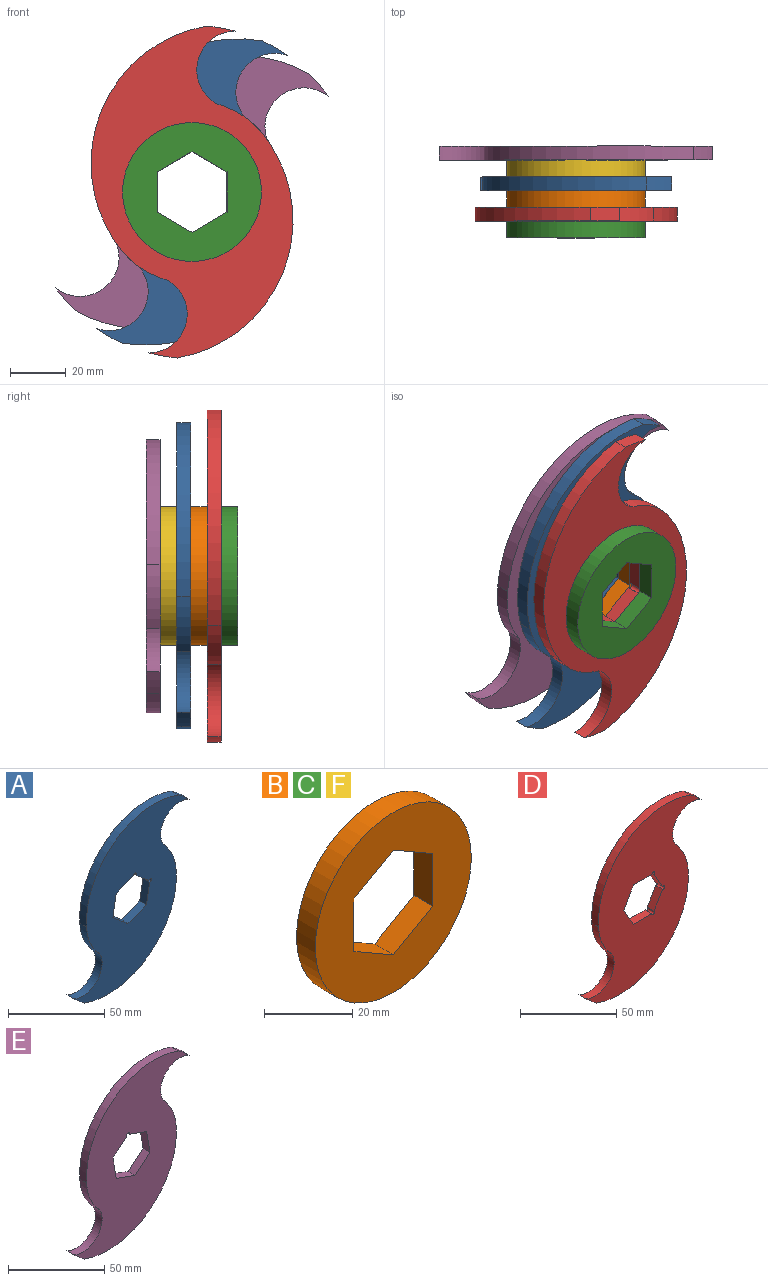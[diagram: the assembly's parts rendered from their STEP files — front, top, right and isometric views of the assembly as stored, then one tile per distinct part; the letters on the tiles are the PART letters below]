
ASSEMBLY  parts=6 mates=4
PART A: 18 faces, bbox 84.9x5x104.4 mm
  f0: plane 9.61x8.07mm, normal (-0.64,0,-0.77), area 62.7mm2, adj f1,f15,f16,f17
  f1: cylinder r=1mm len=5mm, axis (0,1,0), area 20.9mm2, adj f0,f2,f16,f17
  f2: plane 13.34x5mm, normal (-0.98,0,0.17), area 67.7mm2, adj f1,f3,f16,f17
  f3: plane 13.67x5mm, normal (-0.34,0,0.94), area 72.7mm2, adj f2,f4,f16,f17
  f4: plane 11.15x9.35mm, normal (0.64,0,0.77), area 72.7mm2, adj f3,f5,f16,f17
  f5: plane 14.33x5mm, normal (0.98,0,-0.17), area 72.7mm2, adj f4,f6,f16,f17
  f6: plane 12.73x5mm, normal (0.34,0,-0.94), area 67.7mm2, adj f5,f15,f16,f17
  f7: cylinder r=50.21mm len=67.52mm, axis (0,1,0), area 500.3mm2, adj f8,f14,f16,f17
  f8: cylinder r=33mm len=21.82mm, axis (0,1,0), area 122mm2, adj f7,f9,f16,f17
  f9: cylinder r=14.04mm len=20.86mm, axis (0,1,0), area 181.5mm2, adj f8,f10,f16,f17
  f10: cylinder r=60mm len=8mm, axis (0,1,0), area 52.3mm2, adj f9,f11,f16,f17
  f11: cylinder r=50.21mm len=67.52mm, axis (0,1,0), area 500.3mm2, adj f10,f12,f16,f17
  f12: cylinder r=33mm len=21.82mm, axis (0,1,0), area 122mm2, adj f11,f13,f16,f17
  f13: cylinder r=14.04mm len=20.86mm, axis (0,1,0), area 181.5mm2, adj f12,f14,f16,f17
  f14: cylinder r=60mm len=8mm, axis (0,1,0), area 52.3mm2, adj f7,f13,f16,f17
  f15: cylinder r=1mm len=5mm, axis (0,1,0), area 20.9mm2, adj f0,f6,f16,f17
  f16: plane 104.43x84.85mm, normal (0,-1,0), area 4764.9mm2, adj f0,f1,f2,f3,f4,f5,f6,f7
  f17: plane 104.43x84.85mm, normal (0,1,0), area 4764.9mm2, adj f0,f1,f2,f3,f4,f5,f6,f7
PART B: 9 faces, bbox 50x6x50 mm
  f0: plane 12.6x7.27mm, normal (0.5,0,-0.87), area 87.3mm2, adj f1,f6,f7,f8
  f1: plane 12.6x7.27mm, normal (-0.5,0,-0.87), area 87.3mm2, adj f0,f2,f7,f8
  f2: plane 14.55x6mm, normal (-1,0,0), area 87.3mm2, adj f1,f3,f7,f8
  f3: plane 12.6x7.27mm, normal (-0.5,0,0.87), area 87.3mm2, adj f2,f4,f7,f8
  f4: plane 12.6x7.27mm, normal (0.5,0,0.87), area 87.3mm2, adj f3,f6,f7,f8
  f5: cylinder r=25mm len=50mm, axis (0,1,0), area 942.5mm2, adj f7,f8
  f6: plane 14.55x6mm, normal (1,0,0), area 87.3mm2, adj f0,f4,f7,f8
  f7: plane 50x50mm, normal (0,-1,0), area 1413.5mm2, adj f0,f1,f2,f3,f4,f5,f6
  f8: plane 50x50mm, normal (0,1,0), area 1413.5mm2, adj f0,f1,f2,f3,f4,f5,f6
PART C: same geometry as B
PART D: 19 faces, bbox 84.9x5x104.4 mm
  f0: plane 10.87x6.27mm, normal (-0.87,0,-0.5), area 62.7mm2, adj f1,f16,f17,f18
  f1: cylinder r=1mm len=5mm, axis (0,1,0), area 20.9mm2, adj f0,f2,f17,f18
  f2: plane 10.87x6.27mm, normal (-0.87,0,0.5), area 62.7mm2, adj f1,f3,f17,f18
  f3: cylinder r=1mm len=5mm, axis (0,1,0), area 20.9mm2, adj f2,f4,f17,f18
  f4: plane 13.55x5mm, normal (0,0,1), area 67.7mm2, adj f3,f5,f17,f18
  f5: plane 12.6x7.27mm, normal (0.87,0,0.5), area 72.7mm2, adj f4,f6,f17,f18
  f6: plane 12.6x7.27mm, normal (0.87,0,-0.5), area 72.7mm2, adj f5,f7,f17,f18
  f7: plane 13.55x5mm, normal (0,0,-1), area 67.7mm2, adj f6,f16,f17,f18
  f8: cylinder r=14.04mm len=20.86mm, axis (0,1,0), area 181.5mm2, adj f9,f15,f17,f18
  f9: cylinder r=60mm len=8mm, axis (0,1,0), area 52.3mm2, adj f8,f10,f17,f18
  f10: cylinder r=50.21mm len=67.52mm, axis (0,1,0), area 500.3mm2, adj f9,f11,f17,f18
  f11: cylinder r=33mm len=21.82mm, axis (0,1,0), area 122mm2, adj f10,f12,f17,f18
  f12: cylinder r=14.04mm len=20.86mm, axis (0,1,0), area 181.5mm2, adj f11,f13,f17,f18
  f13: cylinder r=60mm len=8mm, axis (0,1,0), area 52.3mm2, adj f12,f14,f17,f18
  f14: cylinder r=50.21mm len=67.52mm, axis (0,1,0), area 500.3mm2, adj f13,f15,f17,f18
  f15: cylinder r=33mm len=21.82mm, axis (0,1,0), area 122mm2, adj f8,f14,f17,f18
  f16: cylinder r=1mm len=5mm, axis (0,1,0), area 20.9mm2, adj f0,f7,f17,f18
  f17: plane 104.43x84.85mm, normal (0,-1,0), area 4762.8mm2, adj f0,f1,f2,f3,f4,f5,f6,f7
  f18: plane 104.43x84.85mm, normal (0,1,0), area 4762.8mm2, adj f0,f1,f2,f3,f4,f5,f6,f7
PART E: 17 faces, bbox 84.9x5x104.4 mm
  f0: plane 10.38x8.71mm, normal (0.64,0,-0.77), area 67.7mm2, adj f1,f14,f15,f16
  f1: cylinder r=1mm len=5mm, axis (0,1,0), area 20.9mm2, adj f0,f2,f15,f16
  f2: plane 12.73x5mm, normal (-0.34,0,-0.94), area 67.7mm2, adj f1,f3,f15,f16
  f3: plane 14.33x5mm, normal (-0.98,0,-0.17), area 72.7mm2, adj f2,f4,f15,f16
  f4: plane 11.15x9.35mm, normal (-0.64,0,0.77), area 72.7mm2, adj f3,f5,f15,f16
  f5: plane 13.67x5mm, normal (0.34,0,0.94), area 72.7mm2, adj f4,f14,f15,f16
  f6: cylinder r=50.21mm len=67.52mm, axis (0,1,0), area 500.3mm2, adj f7,f13,f15,f16
  f7: cylinder r=33mm len=21.82mm, axis (0,1,0), area 122mm2, adj f6,f8,f15,f16
  f8: cylinder r=14.04mm len=20.86mm, axis (0,1,0), area 181.5mm2, adj f7,f9,f15,f16
  f9: cylinder r=60mm len=8mm, axis (0,1,0), area 52.3mm2, adj f8,f10,f15,f16
  f10: cylinder r=50.21mm len=67.52mm, axis (0,1,0), area 500.3mm2, adj f9,f11,f15,f16
  f11: cylinder r=33mm len=21.82mm, axis (0,1,0), area 122mm2, adj f10,f12,f15,f16
  f12: cylinder r=14.04mm len=20.86mm, axis (0,1,0), area 181.5mm2, adj f11,f13,f15,f16
  f13: cylinder r=60mm len=8mm, axis (0,1,0), area 52.3mm2, adj f6,f12,f15,f16
  f14: plane 14.33x5mm, normal (0.98,0,0.17), area 72.7mm2, adj f0,f5,f15,f16
  f15: plane 104.43x84.85mm, normal (0,-1,0), area 4767mm2, adj f0,f1,f2,f3,f4,f5,f6,f7
  f16: plane 104.43x84.85mm, normal (0,1,0), area 4767mm2, adj f0,f1,f2,f3,f4,f5,f6,f7
PART F: same geometry as B
PLACE A rot(axis=(0,-1,0),10deg) t=(-16.87,7.86,-47.55)mm
PLACE B t=(-16.89,2.86,-47.56)mm
PLACE C rot(axis=(0,1,0),0deg) t=(-16.88,-8.14,-47.55)mm
PLACE D rot(axis=(0,-1,0),30deg) t=(-16.88,-3.14,-47.55)mm
PLACE E rot(axis=(0,1,0),10deg) t=(-16.88,18.86,-47.61)mm
PLACE F t=(-16.88,13.86,-47.56)mm
MATE pin_slot D.f18 <-> B.f5  axis (0,1,0) through (-16.89,-3.14,-47.56)mm
MATE pin_slot A.f17 <-> F.f5  axis (0,1,0) through (-16.87,7.86,-47.56)mm
MATE pin_slot B.f5 <-> A.f16  axis (0,1,0) through (-16.89,2.86,-47.56)mm
MATE pin_slot C.f5 <-> D.f17  axis (0,1,0) through (-16.88,-8.14,-47.55)mm
